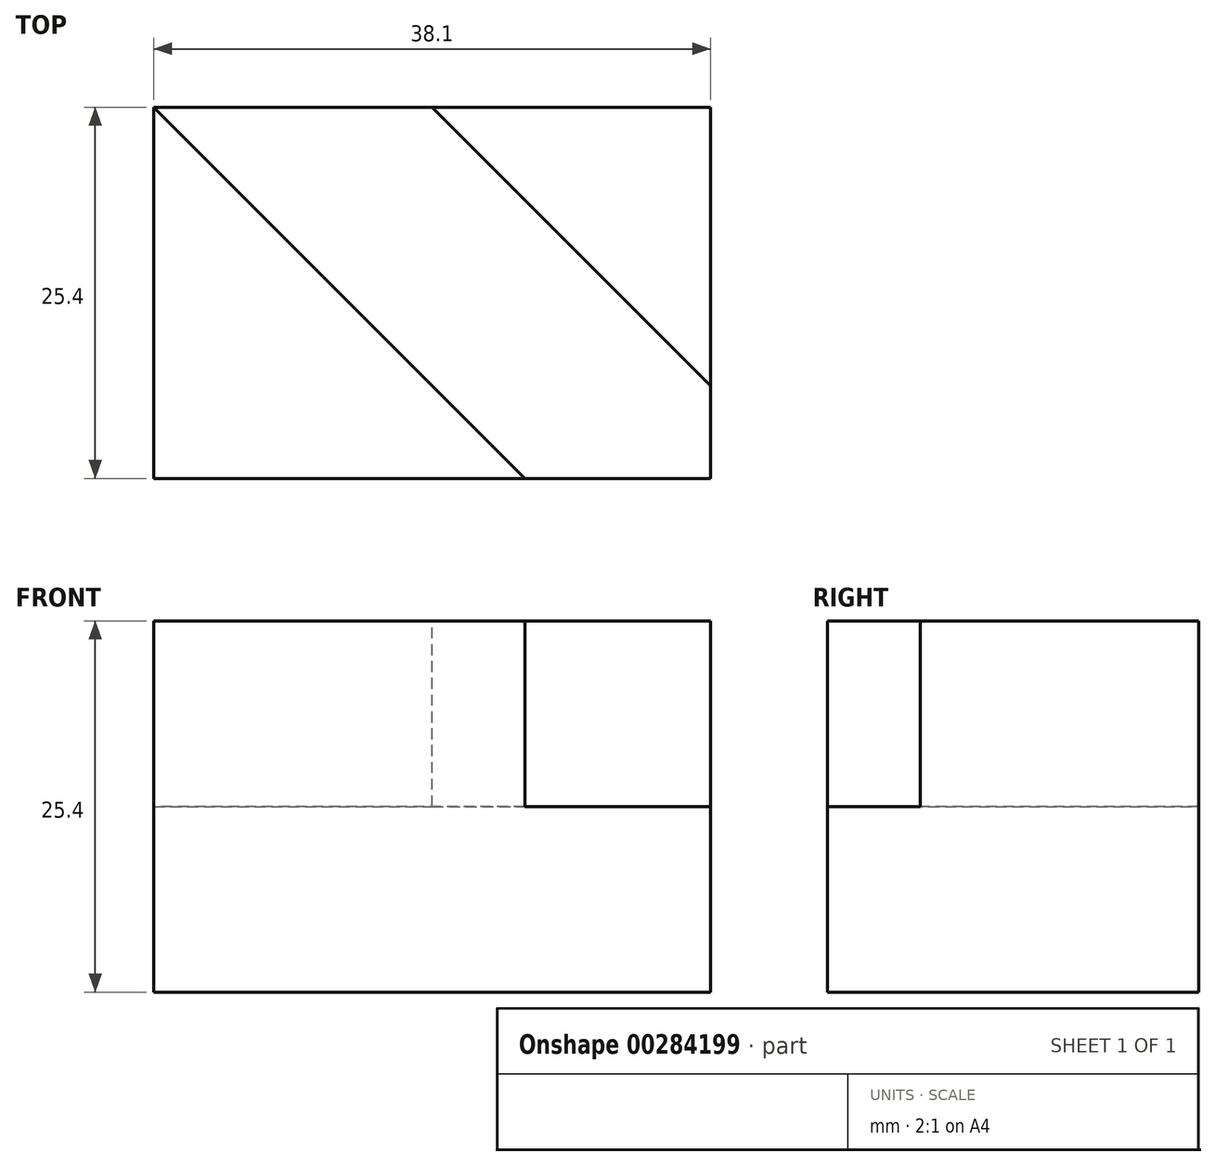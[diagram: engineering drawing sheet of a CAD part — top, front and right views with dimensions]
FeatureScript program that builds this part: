
annotation { "Feature Type Name" : "Feature", "Feature Type Description" : "" }
export const myFeature = defineFeature(function(context is Context, id is Id, definition is map)
    precondition{}
    {
        {
            var Q0;
            Q0=qCreatedBy(makeId("Front.planeOp"),FACE);
            var sketch = newSketch(context, id + "F0", { "sketchPlane" : qUnion([Q0])});
            skLineSegment(sketch, "E0", {"start": v(0, 0) * mm, "end": v(0, 25.4) * mm});
            skLineSegment(sketch, "E1", {"start": v(0, 25.4) * mm, "end": v(38.1, 25.4) * mm});
            skLineSegment(sketch, "E2", {"start": v(38.1, 25.4) * mm, "end": v(38.1, 0) * mm});
            skLineSegment(sketch, "E3", {"start": v(38.1, 0) * mm, "end": v(0, 0) * mm});
            skSolve(sketch);
        }
        {
            var Q0;
            Q0=makeQuery(id+"F0.imprint","IMPRINT",FACE,{"disambiguationData":[TD([[makeQuery(id+"F0.imprint","IMPRINT",EDGE,{"derivedFrom":sQuery(id+"F0.wireOp",EDGE,"E0")}),-1.0]])]});
            extrude(context, id + "F1", {"entities" : qUnion([Q0]), "depth" : 25.4 * mm});
        }
        {
            var Q0;
            Q0=makeQuery(id+"F1.opExtrude","SWEPT_FACE",FACE,{"disambiguationData":[OSD([sQuery(id+"F0.wireOp",EDGE,"E2")])]});
            var sketch = newSketch(context, id + "F2", { "sketchPlane" : qUnion([Q0])});
            skLineSegment(sketch, "E4", {"start": v(-25.4, 25.4) * mm, "end": v(-19.05, 25.4) * mm});
            skLineSegment(sketch, "E5", {"start": v(-19.05, 25.4) * mm, "end": v(-19.05, 12.7) * mm});
            skLineSegment(sketch, "E6", {"start": v(-19.05, 12.7) * mm, "end": v(-25.4, 12.7) * mm});
            skLineSegment(sketch, "E7", {"start": v(-25.4, 12.7) * mm, "end": v(-25.4, 25.4) * mm});
            skSolve(sketch);
        }
        {
            var Q0;
            Q0=makeQuery(id+"F2.imprint","IMPRINT",FACE,{"disambiguationData":[TD([[makeQuery(id+"F2.imprint","IMPRINT",EDGE,{"derivedFrom":sQuery(id+"F2.wireOp",EDGE,"E4")}),-1.0]])]});
            extrude(context, id + "F3", {"entities" : qUnion([Q0]), "operationType" : NewBodyOperationType.REMOVE, "oppositeDirection" : true, "depth" : 12.7 * mm});
        }
        {
            var Q0;
            Q0=makeQuery(id+"F1.opExtrude","SWEPT_FACE",FACE,{"disambiguationData":[OSD([sQuery(id+"F0.wireOp",EDGE,"E1")])]});
            var sketch = newSketch(context, id + "F4", { "sketchPlane" : qUnion([Q0])});
            skLineSegment(sketch, "E8", {"start": v(25.4, -25.4) * mm, "end": v(0, 0) * mm});
            skLineSegment(sketch, "E9", {"start": v(0, 0) * mm, "end": v(19.05, 0) * mm});
            skLineSegment(sketch, "E10", {"start": v(19.05, 0) * mm, "end": v(38.1, -19.05) * mm});
            skLineSegment(sketch, "E11", {"start": v(38.1, -19.05) * mm, "end": v(25.4, -19.05) * mm});
            skLineSegment(sketch, "E12", {"start": v(25.4, -19.05) * mm, "end": v(25.4, -25.4) * mm});
            skSolve(sketch);
        }
        {
            var Q0;
            Q0=makeQuery(id+"F4.imprint","IMPRINT",FACE,{"disambiguationData":[TD([[makeQuery(id+"F4.imprint","IMPRINT",EDGE,{"derivedFrom":sQuery(id+"F4.wireOp",EDGE,"E8")}),-1.0]])]});
            extrude(context, id + "F5", {"entities" : qUnion([Q0]), "operationType" : NewBodyOperationType.REMOVE, "oppositeDirection" : true, "depth" : 12.7 * mm});
        }
    });
